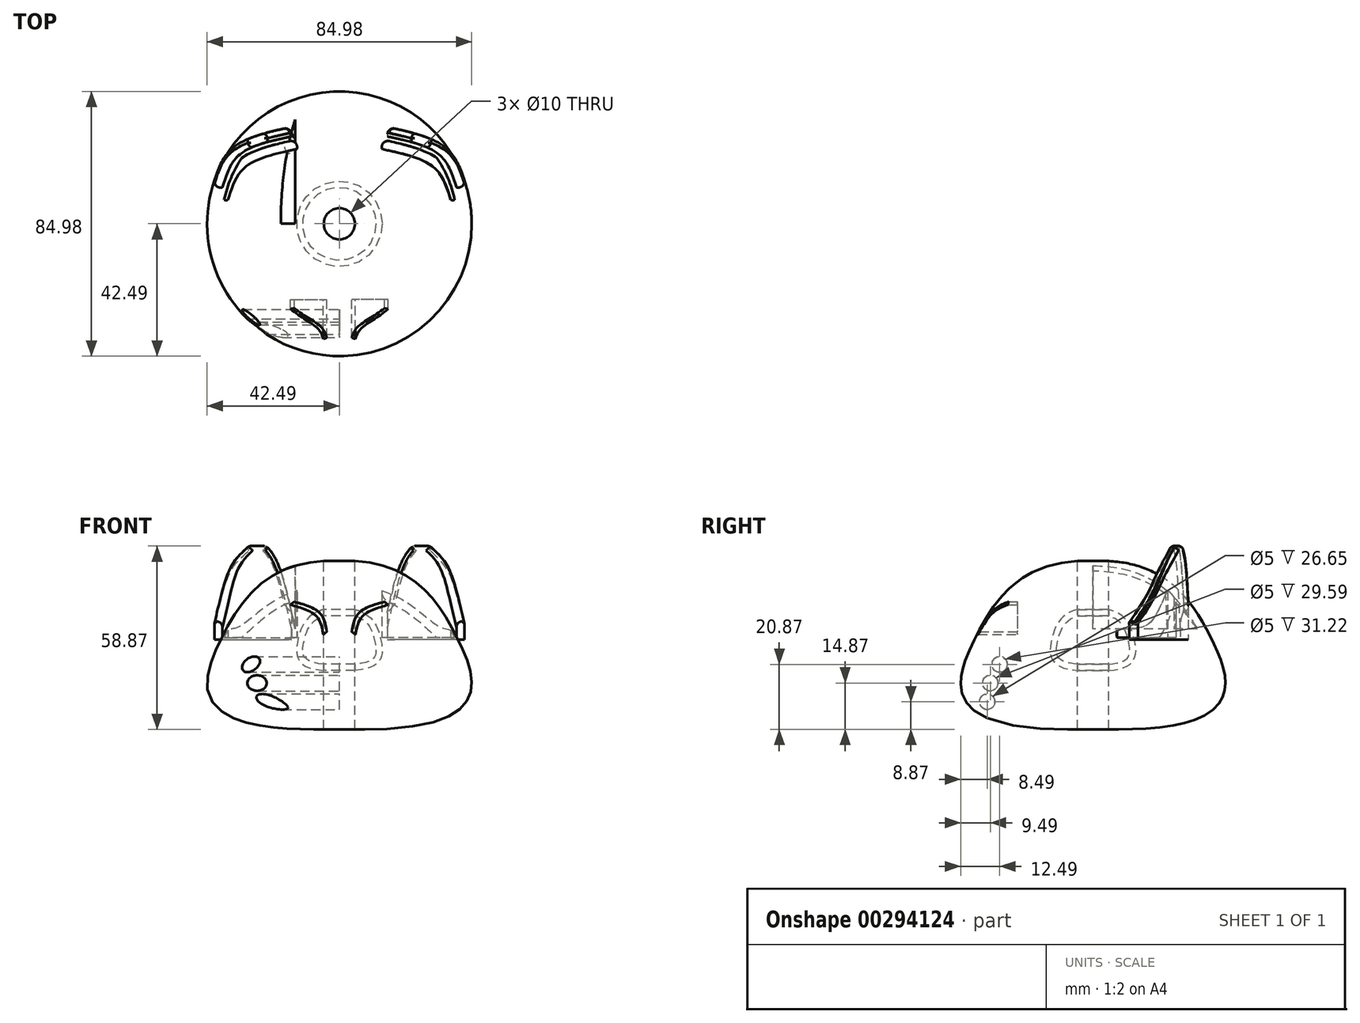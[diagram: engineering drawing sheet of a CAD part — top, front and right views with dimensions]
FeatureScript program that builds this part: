
annotation { "Feature Type Name" : "Feature", "Feature Type Description" : "" }
export const myFeature = defineFeature(function(context is Context, id is Id, definition is map)
    precondition{}
    {
        {
            var Q0;
            Q0=qCreatedBy(makeId("Front.planeOp"),FACE);
            var sketch = newSketch(context, id + "F0", { "sketchPlane" : qUnion([Q0])});
            skLineSegment(sketch, "E0", {"start": v(0, 10.17) * mm, "end": v(0, -9.83) * mm});
            skFitSpline(sketch, "E1", {"points": [v(0, 10.17) * mm, v(-13.28, 0) * mm, v(0, -9.83) * mm], "startDerivative": vector(-58.45, 0) * mm, "endDerivative": vector(87.07, 6.28) * mm});
            skSolve(sketch);
        }
        {
            var Q0;
            Q0 = qSketchRegion(id + "F0", true);
            var Q1;
            Q1=sQuery(id+"F0.wireOp",EDGE,"E0");
            revolve(context, id + "F1", {"entities" : qUnion([Q0]), "axis" : qUnion([Q1]), "revolveType" : RevolveType.FULL});
        }
        {
            var Q0;
            Q0=qCreatedBy(makeId("Top.planeOp"),FACE);
            var sketch = newSketch(context, id + "F2", { "sketchPlane" : qUnion([Q0])});
            skCircle(sketch, "E2", {"center": v(0, 0) * mm, "radius": 5 * mm});
            skSolve(sketch);
        }
        {
            var Q0;
            Q0 = qSketchRegion(id + "F2", true);
            extrude(context, id + "F3", {"entities" : qUnion([Q0]), "operationType" : NewBodyOperationType.REMOVE, "endBound" : BoundingType.SYMMETRIC, "depth" : 35.2 * mm});
        }
        {
            var Q0;
            Q0=makeQuery(id+"F3.boolean.opBoolean","COPY",FACE,{"derivedFrom":makeQuery(id+"F3.opExtrude","SWEPT_FACE",FACE,{"disambiguationData":[OSD([sQuery(id+"F2.wireOp",EDGE,"E2")])]})});
            shell(context, id + "F4", {"entities" : qUnion([Q0]), "thickness" : 2 * mm});
        }
        {
            var Q0;
            Q0=qCreatedBy(makeId("Front.planeOp"),FACE);
            var sketch = newSketch(context, id + "F5", { "sketchPlane" : qUnion([Q0])});
            skFitSpline(sketch, "E3", {"points": [v(0, 25.19) * mm, v(-38.1, 0) * mm, v(0, -28.7) * mm], "startDerivative": vector(-134.4, 5.8) * mm, "endDerivative": vector(297.11, 12.33) * mm});
            skLineSegment(sketch, "E4", {"start": v(0, 25.19) * mm, "end": v(0, -28.7) * mm});
            skSolve(sketch);
        }
        {
            var Q0;
            Q0=makeQuery(id+"F5.imprint","IMPRINT",FACE,{"disambiguationData":[TD([[makeQuery(id+"F5.imprint","IMPRINT",EDGE,{"derivedFrom":sQuery(id+"F5.wireOp",EDGE,"E3")}),1.0]])]});
            var Q1;
            Q1=sQuery(id+"F5.wireOp",EDGE,"E4");
            revolve(context, id + "F6", {"entities" : qUnion([Q0]), "axis" : qUnion([Q1]), "revolveType" : RevolveType.FULL});
        }
        {
            var Q0;
            Q0=qCreatedBy(makeId("Top.planeOp"),FACE);
            var sketch = newSketch(context, id + "F7", { "sketchPlane" : qUnion([Q0])});
            skCircle(sketch, "E5", {"center": v(0, 0) * mm, "radius": 5 * mm});
            skSolve(sketch);
        }
        {
            var Q0;
            Q0 = qSketchRegion(id + "F7", true);
            var Q1;
            Q1 = qConstructionFilter(qBodyType(qCreatedBy(id + "F7" ,EDGE), BodyType.WIRE), ConstructionObject.NO);
            extrude(context, id + "F8", {"entities" : qUnion([Q0]), "operationType" : NewBodyOperationType.REMOVE, "surfaceEntities" : qUnion([Q1]), "endBound" : BoundingType.SYMMETRIC, "oppositeDirection" : true, "depth" : 74.8 * mm});
        }
        {
            var Q0;
            Q0=qCreatedBy(makeId("Front.planeOp"),FACE);
            var sketch = newSketch(context, id + "F9", { "sketchPlane" : qUnion([Q0])});
            skFitSpline(sketch, "E6", {"points": [v(-14.5, 12.12) * mm, v(-6.22, 8.45) * mm, v(-3.99, 2.55) * mm], "startDerivative": vector(18.01, -5.02) * mm, "endDerivative": vector(2.57, -14.39) * mm});
            skFitSpline(sketch, "E7", {"points": [v(-15.68, 11.1) * mm, v(-7.4, 7.44) * mm, v(-5.16, 1.54) * mm], "startDerivative": vector(18.01, -5.02) * mm, "endDerivative": vector(2.57, -14.39) * mm});
            skLineSegment(sketch, "E8", {"start": v(-15.68, 11.1) * mm, "end": v(-14.5, 12.12) * mm});
            skLineSegment(sketch, "E9", {"start": v(-5.16, 1.54) * mm, "end": v(-3.99, 2.55) * mm});
            skFitSpline(sketch, "E10.MirrorCS", {"points": [v(14.5, 12.12) * mm, v(6.22, 8.45) * mm, v(3.99, 2.55) * mm], "startDerivative": vector(-18.01, -5.02) * mm, "endDerivative": vector(-2.57, -14.39) * mm});
            skFitSpline(sketch, "E11.MirrorCS", {"points": [v(15.68, 11.1) * mm, v(7.4, 7.44) * mm, v(5.16, 1.54) * mm], "startDerivative": vector(-18.01, -5.02) * mm, "endDerivative": vector(-2.57, -14.39) * mm});
            skLineSegment(sketch, "E12.MirrorCS", {"start": v(15.68, 11.1) * mm, "end": v(14.5, 12.12) * mm});
            skLineSegment(sketch, "E13.MirrorCS", {"start": v(5.16, 1.54) * mm, "end": v(3.99, 2.55) * mm});
            skSolve(sketch);
        }
        {
            var Q0;
            Q0 = qSketchRegion(id + "F9", true);
            extrude(context, id + "F10", {"entities" : qUnion([Q0]), "operationType" : NewBodyOperationType.REMOVE, "depth" : 44.3 * mm, "hasSecondDirection" : true, "secondDirectionOppositeDirection" : false, "secondDirectionDepth" : 24.3 * mm});
        }
        {
            var Q0;
            Q0=qCreatedBy(makeId("Top.planeOp"),FACE);
            var sketch = newSketch(context, id + "F11", { "sketchPlane" : qUnion([Q0])});
            skFitSpline(sketch, "E14", {"points": [v(-35.78, 7.68) * mm, v(-30.45, 18.01) * mm, v(-13.65, 24) * mm], "startDerivative": vector(8.2, 25.12) * mm, "endDerivative": vector(34.83, 7.71) * mm});
            skFitSpline(sketch, "E15", {"points": [v(-38.22, 10.34) * mm, v(-32.52, 20.26) * mm, v(-15.98, 26.54) * mm], "startDerivative": vector(8.2, 25.12) * mm, "endDerivative": vector(34.83, 7.71) * mm});
            skArc(sketch, "E16", {"start": v(-13.65, 24) * mm, "mid": v(-14.1, 25.94) * mm, "end": v(-15.98, 26.54) * mm});
            skArc(sketch, "E17", {"start": v(-38.22, 10.34) * mm, "mid": v(-37.84, 8.24) * mm, "end": v(-35.78, 7.68) * mm});
            skFitSpline(sketch, "E18.MirrorCS", {"points": [v(35.78, 7.68) * mm, v(30.45, 18.01) * mm, v(13.65, 24) * mm], "startDerivative": vector(-8.2, 25.12) * mm, "endDerivative": vector(-34.83, 7.71) * mm});
            skArc(sketch, "E19.MirrorCS", {"start": v(38.22, 10.34) * mm, "mid": v(37.84, 8.24) * mm, "end": v(35.78, 7.68) * mm});
            skFitSpline(sketch, "E20.MirrorCS", {"points": [v(38.22, 10.34) * mm, v(32.52, 20.26) * mm, v(15.98, 26.54) * mm], "startDerivative": vector(-8.2, 25.12) * mm, "endDerivative": vector(-34.83, 7.71) * mm});
            skArc(sketch, "E21.MirrorCS", {"start": v(13.65, 24) * mm, "mid": v(14.1, 25.94) * mm, "end": v(15.98, 26.54) * mm});
            skSolve(sketch);
        }
        {
            var Q0;
            Q0 = qSketchRegion(id + "F11", true);
            extrude(context, id + "F12", {"entities" : qUnion([Q0]), "operationType" : NewBodyOperationType.REMOVE, "depth" : 17.3 * mm, "hasSecondDirection" : true, "secondDirectionOppositeDirection" : false, "secondDirectionDepth" : 0.6 * mm});
        }
        {
            var Q0;
            Q0=qCreatedBy(makeId("Top.planeOp"),FACE);
            var sketch = newSketch(context, id + "F13", { "sketchPlane" : qUnion([Q0])});
            skFitSpline(sketch, "E22", {"points": [v(-37.57, 11.7) * mm, v(-32.24, 22.04) * mm, v(-15.44, 28.04) * mm], "startDerivative": vector(8.2, 25.12) * mm, "endDerivative": vector(34.83, 7.71) * mm});
            skFitSpline(sketch, "E23", {"points": [v(-40, 14.37) * mm, v(-34.3, 24.3) * mm, v(-17.77, 30.57) * mm], "startDerivative": vector(8.2, 25.12) * mm, "endDerivative": vector(34.83, 7.71) * mm});
            skArc(sketch, "E24", {"start": v(-15.44, 28.04) * mm, "mid": v(-15.89, 29.97) * mm, "end": v(-17.77, 30.57) * mm});
            skArc(sketch, "E25", {"start": v(-40, 14.37) * mm, "mid": v(-39.63, 12.27) * mm, "end": v(-37.57, 11.7) * mm});
            skSolve(sketch);
        }
        {
            var Q0;
            Q0 = qSketchRegion(id + "F13", true);
            extrude(context, id + "F14", {"entities" : qUnion([Q0]), "depth" : 30 * mm});
        }
        {
            var Q0;
            Q0=qCreatedBy(makeId("Front.planeOp"),FACE);
            var sketch = newSketch(context, id + "F15", { "sketchPlane" : qUnion([Q0])});
            skLineSegment(sketch, "E26", {"start": v(-40.55, 3.38) * mm, "end": v(-40.55, 32.33) * mm});
            skLineSegment(sketch, "E27", {"start": v(-40.55, 32.33) * mm, "end": v(-26.53, 32.2) * mm});
            skLineSegment(sketch, "E28", {"start": v(-14.17, 3.38) * mm, "end": v(-14.17, 32.2) * mm});
            skLineSegment(sketch, "E29", {"start": v(-14.17, 32.2) * mm, "end": v(-26.53, 32.2) * mm});
            skFitSpline(sketch, "E30", {"points": [v(-26.53, 32.2) * mm, v(-40.55, 3.38) * mm], "startDerivative": vector(-27, -23.81) * mm, "endDerivative": vector(-15.08, -64.8) * mm});
            skFitSpline(sketch, "E31", {"points": [v(-26.53, 32.2) * mm, v(-14.17, 3.38) * mm], "startDerivative": vector(21.2, -12.17) * mm, "endDerivative": vector(12.13, -53.7) * mm});
            skSolve(sketch);
        }
        {
            var Q0;
            Q0 = qSketchRegion(id + "F15", true);
            extrude(context, id + "F16", {"entities" : qUnion([Q0]), "operationType" : NewBodyOperationType.REMOVE, "oppositeDirection" : true, "depth" : 48.6 * mm});
        }
        {
            var Q0;
            Q0=makeQuery(id+"F14.opExtrude","CAP_FACE",FACE,{"disambiguationData":[OSD([sQuery(id+"F13.wireOp",EDGE,"E22"),sQuery(id+"F13.wireOp",EDGE,"E23"),sQuery(id+"F13.wireOp",EDGE,"E24"),sQuery(id+"F13.wireOp",EDGE,"E25")])],"isStart":false});
            var Q1;
            Q1=makeQuery(id+"F16.boolean.opBoolean","COPY",FACE,{"derivedFrom":makeQuery(id+"F16.opExtrude","SWEPT_FACE",FACE,{"disambiguationData":[OSD([sQuery(id+"F15.wireOp",EDGE,"E30")])]})});
            var Q2;
            Q2=makeQuery(id+"F16.boolean.opBoolean","COPY",FACE,{"derivedFrom":makeQuery(id+"F16.opExtrude","SWEPT_FACE",FACE,{"disambiguationData":[OSD([sQuery(id+"F15.wireOp",EDGE,"E31")])]})});
            fillet(context, id + "F17", {"entities" : qUnion([Q0, Q1, Q2]), "radius" : 1.46 * mm, "tangentPropagation" : true, "allowEdgeOverflow" : false});
        }
        {
            var Q0;
            Q0=makeQuery(id+"F14.opExtrude","SWEPT_BODY",BODY,{"disambiguationData":[OSD([sQuery(id+"F13.wireOp",EDGE,"E22"),sQuery(id+"F13.wireOp",EDGE,"E23"),sQuery(id+"F13.wireOp",EDGE,"E24"),sQuery(id+"F13.wireOp",EDGE,"E25")])]});
            var Q1;
            Q1=qCreatedBy(makeId("Right.planeOp"),FACE);
            mirror(context, id + "F18", {"entities" : qUnion([Q0]), "mirrorPlane" : qUnion([Q1])});
        }
        {
            var Q0;
            Q0=qCreatedBy(makeId("Right.planeOp"),FACE);
            var sketch = newSketch(context, id + "F19", { "sketchPlane" : qUnion([Q0])});
            skCircle(sketch, "E32", {"center": v(-30, -8) * mm, "radius": 2.5 * mm});
            skCircle(sketch, "E33", {"center": v(-33, -14) * mm, "radius": 2.5 * mm});
            skCircle(sketch, "E34", {"center": v(-34, -20) * mm, "radius": 2.5 * mm});
            skSolve(sketch);
        }
        {
            var Q0;
            Q0 = qSketchRegion(id + "F19", true);
            extrude(context, id + "F20", {"entities" : qUnion([Q0]), "operationType" : NewBodyOperationType.REMOVE, "oppositeDirection" : true, "depth" : 55.6 * mm});
        }
    });
